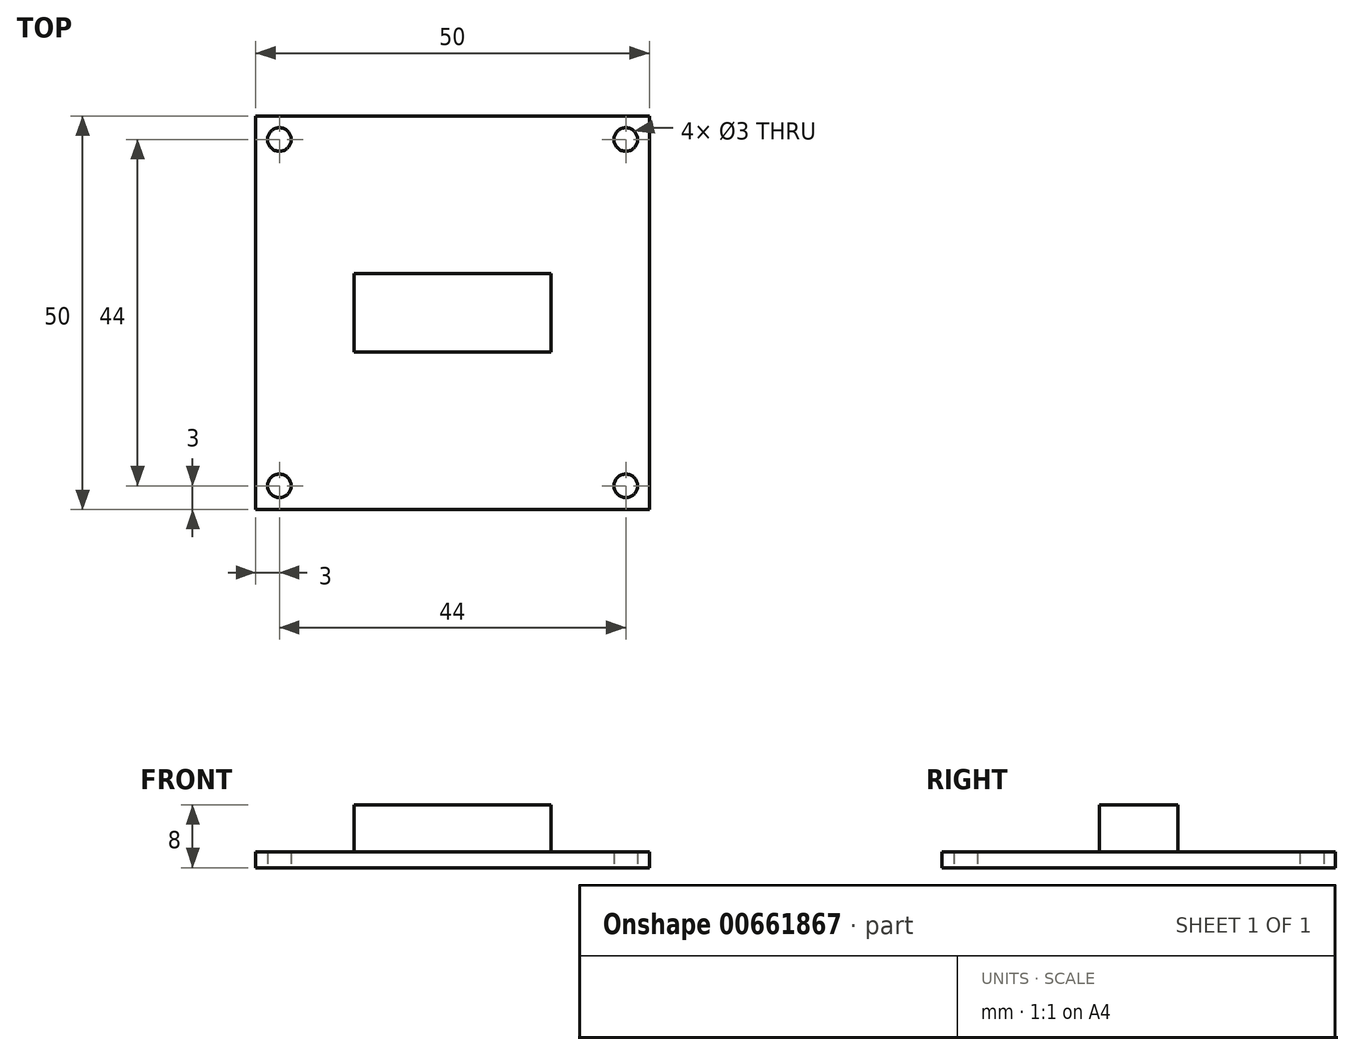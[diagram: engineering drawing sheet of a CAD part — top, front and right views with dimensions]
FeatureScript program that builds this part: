
annotation { "Feature Type Name" : "Feature", "Feature Type Description" : "" }
export const myFeature = defineFeature(function(context is Context, id is Id, definition is map)
    precondition{}
    {
        {
            var Q0;
            Q0=qCreatedBy(makeId("Top.planeOp"),FACE);
            var sketch = newSketch(context, id + "F0", { "sketchPlane" : qUnion([Q0])});
            skLineSegment(sketch, "E0.bottom", {"start": v(25, 25) * mm, "end": v(-25, 25) * mm});
            skLineSegment(sketch, "E0.top", {"start": v(25, -25) * mm, "end": v(-25, -25) * mm});
            skLineSegment(sketch, "E0.left", {"start": v(25, 25) * mm, "end": v(25, -25) * mm});
            skLineSegment(sketch, "E0.right", {"start": v(-25, 25) * mm, "end": v(-25, -25) * mm});
            skPoint(sketch, "E0.middle", {"position": v(0, 0) * mm});
            skSolve(sketch);
        }
        {
            var Q0;
            Q0 = qSketchRegion(id + "F0", true);
            extrude(context, id + "F1", {"entities" : qUnion([Q0]), "depth" : 2 * mm, "offsetDistance" : 25 * mm});
        }
        {
            var Q0;
            Q0=qCreatedBy(makeId("Top.planeOp"),FACE);
            var sketch = newSketch(context, id + "F2", { "sketchPlane" : qUnion([Q0])});
            skCircle(sketch, "E1", {"center": v(-22, 22) * mm, "radius": 1.5 * mm});
            skLineSegment(sketch, "E2", {"start": v(-22, 22) * mm, "end": v(-25, 22) * mm, "construction": true});
            skLineSegment(sketch, "E3", {"start": v(-22, 22) * mm, "end": v(-22, 25) * mm, "construction": true});
            skCircle(sketch, "E4.1.0", {"center": v(-22, -22) * mm, "radius": 1.5 * mm});
            skCircle(sketch, "E4.2.0", {"center": v(22, -22) * mm, "radius": 1.5 * mm});
            skCircle(sketch, "E4.3.0", {"center": v(22, 22) * mm, "radius": 1.5 * mm});
            skPoint(sketch, "E4.center", {"position": v(0, 0) * mm});
            skSolve(sketch);
        }
        {
            var Q0;
            Q0 = qSketchRegion(id + "F2", true);
            extrude(context, id + "F3", {"entities" : qUnion([Q0]), "operationType" : NewBodyOperationType.REMOVE, "endBound" : BoundingType.THROUGH_ALL, "depth" : 25 * mm, "offsetDistance" : 25 * mm});
        }
        {
            var Q0;
            Q0=makeQuery(id+"F1.opExtrude","CAP_FACE",FACE,{"disambiguationData":[OSD([sQuery(id+"F0.wireOp",EDGE,"E0.bottom"),sQuery(id+"F0.wireOp",EDGE,"E0.top"),sQuery(id+"F0.wireOp",EDGE,"E0.left"),sQuery(id+"F0.wireOp",EDGE,"E0.right")])],"isStart":false});
            var sketch = newSketch(context, id + "F4", { "sketchPlane" : qUnion([Q0])});
            skLineSegment(sketch, "E5.bottom", {"start": v(-12.5, 5) * mm, "end": v(12.5, 5) * mm});
            skLineSegment(sketch, "E5.top", {"start": v(-12.5, -5) * mm, "end": v(12.5, -5) * mm});
            skLineSegment(sketch, "E5.left", {"start": v(-12.5, 5) * mm, "end": v(-12.5, -5) * mm});
            skLineSegment(sketch, "E5.right", {"start": v(12.5, 5) * mm, "end": v(12.5, -5) * mm});
            skPoint(sketch, "E5.middle", {"position": v(0, 0) * mm});
            skSolve(sketch);
        }
        {
            var Q0;
            Q0 = qSketchRegion(id + "F4", true);
            extrude(context, id + "F5", {"entities" : qUnion([Q0]), "operationType" : NewBodyOperationType.ADD, "depth" : 6 * mm, "offsetDistance" : 25 * mm});
        }
    });
